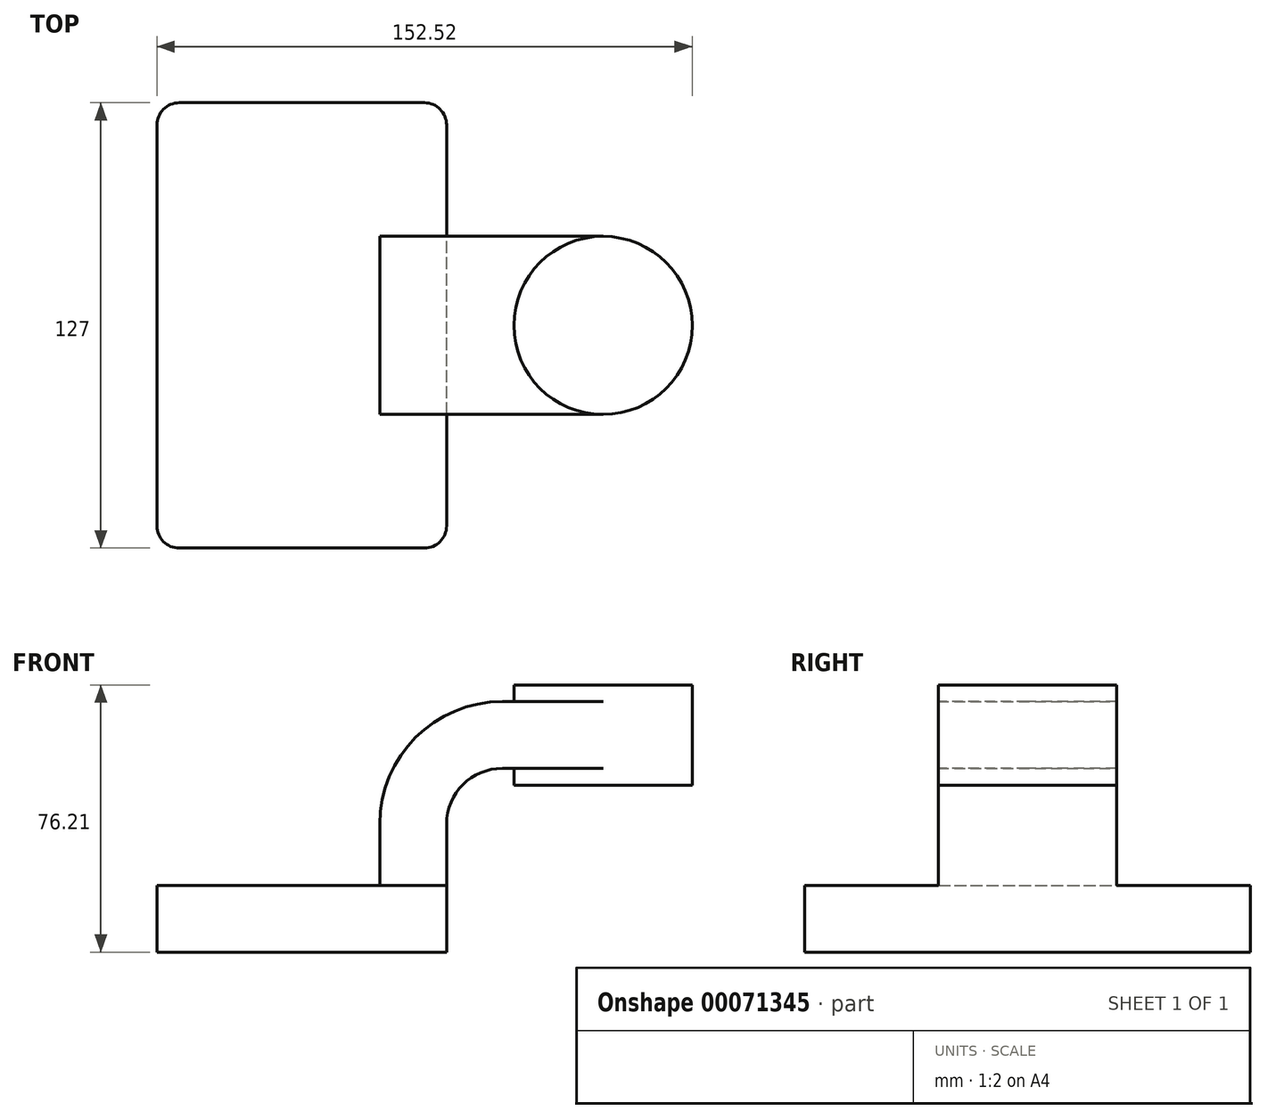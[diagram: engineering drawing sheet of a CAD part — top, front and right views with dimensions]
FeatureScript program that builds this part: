
annotation { "Feature Type Name" : "Feature", "Feature Type Description" : "" }
export const myFeature = defineFeature(function(context is Context, id is Id, definition is map)
    precondition{}
    {
        {
            var Q0;
            Q0=qCreatedBy(makeId("Front.planeOp"),FACE);
            var sketch = newSketch(context, id + "F0", { "sketchPlane" : qUnion([Q0])});
            skLineSegment(sketch, "E0.rect.bottom", {"start": v(41.28, -9.52) * mm, "end": v(-41.28, -9.53) * mm});
            skLineSegment(sketch, "E0.rect.top", {"start": v(41.28, 9.53) * mm, "end": v(-41.28, 9.53) * mm});
            skLineSegment(sketch, "E0.rect.left", {"start": v(41.28, -9.52) * mm, "end": v(41.28, 9.53) * mm});
            skLineSegment(sketch, "E0.rect.right", {"start": v(-41.28, -9.53) * mm, "end": v(-41.28, 9.53) * mm});
            skPoint(sketch, "E0.rect.middle", {"position": v(0, 0) * mm});
            skLineSegment(sketch, "E1.rect.bottom", {"start": v(111.25, 38.1) * mm, "end": v(60.45, 38.1) * mm});
            skLineSegment(sketch, "E1.rect.top", {"start": v(111.25, 66.68) * mm, "end": v(60.45, 66.68) * mm});
            skLineSegment(sketch, "E1.rect.left", {"start": v(111.25, 38.1) * mm, "end": v(111.25, 66.68) * mm});
            skLineSegment(sketch, "E1.rect.right", {"start": v(60.45, 38.1) * mm, "end": v(60.45, 66.68) * mm});
            skPoint(sketch, "E1.rect.middle", {"position": v(85.85, 52.39) * mm});
            skLineSegment(sketch, "E2", {"start": v(41.28, 9.53) * mm, "end": v(41.28, 27) * mm});
            skArc(sketch, "E3", {"start": v(41.27, 27) * mm, "mid": v(45.92, 38.23) * mm, "end": v(57.15, 42.88) * mm});
            skLineSegment(sketch, "E4", {"start": v(57.15, 42.88) * mm, "end": v(85.85, 42.88) * mm});
            skLineSegment(sketch, "E5.0", {"start": v(57.15, 61.93) * mm, "end": v(85.85, 61.93) * mm});
            skArc(sketch, "E5.1", {"start": v(22.23, 27) * mm, "mid": v(32.45, 51.7) * mm, "end": v(57.15, 61.93) * mm});
            skLineSegment(sketch, "E5.2", {"start": v(22.22, 9.53) * mm, "end": v(22.22, 27) * mm});
            skLineSegment(sketch, "E6", {"start": v(85.85, 38.1) * mm, "end": v(85.85, 66.68) * mm});
            skFitSpline(sketch, "E7", {"points": [v(-41.28, 9.53) * mm, v(57.15, 61.93) * mm], "startDerivative": vector(0.48, 72.5) * mm, "endDerivative": vector(122.57, -13.34) * mm});
            skSolve(sketch);
        }
        {
            var Q0;
            Q0=makeQuery(id+"F0.imprint","IMPRINT",FACE,{"disambiguationData":[TD([[makeQuery(id+"F0.imprint","IMPRINT",EDGE,{"derivedFrom":sQuery(id+"F0.wireOp",EDGE,"E0.rect.bottom")}),-1.0]])]});
            extrude(context, id + "F1", {"entities" : qUnion([Q0]), "depth" : 127 * mm, "symmetric" : true});
        }
        {
            var Q0;
            {var subQ1=sQuery(id+"F0.wireOp",EDGE,"E2");Q0=makeQuery(id+"F0.imprint","IMPRINT",FACE,{"disambiguationData":[TD([[makeQuery(id+"F0.imprint","IMPRINT",EDGE,{"derivedFrom":subQ1}),1.0]])]});}
            var Q1;
            {var subQ0=sQuery(id+"F0.wireOp",EDGE,"E4");var subQ1=sQuery(id+"F0.wireOp",EDGE,"E1.rect.right");var subQ2=makeQuery(id+"F0.imprint","INTERSECT",VERTEX,{"derivedFrom":[subQ1,subQ0]});Q1=makeQuery(id+"F0.imprint","IMPRINT",FACE,{"disambiguationData":[TD([[makeQuery(id+"F0.imprint","IMPRINT",EDGE,{"disambiguationData":[TD([[subQ2,-1.0]])],"derivedFrom":subQ1}),-1.0]])]});}
            extrude(context, id + "F2", {"entities" : qUnion([Q0, Q1]), "operationType" : NewBodyOperationType.ADD, "depth" : 50.8 * mm, "symmetric" : true});
        }
        {
            var Q0;
            Q0=makeQuery(id+"F0.imprint","IMPRINT",FACE,{"disambiguationData":[TD([[makeQuery(id+"F0.imprint","IMPRINT",EDGE,{"derivedFrom":sQuery(id+"F0.wireOp",EDGE,"E5.1")}),1.0]])]});
            extrude(context, id + "F3", {"entities" : qUnion([Q0]), "operationType" : NewBodyOperationType.ADD, "depth" : 15.88 * mm, "symmetric" : true});
        }
        {
            var Q0;
            {var subQ0=sQuery(id+"F0.wireOp",EDGE,"E1.rect.left");Q0=makeQuery(id+"F0.imprint","IMPRINT",FACE,{"disambiguationData":[TD([[makeQuery(id+"F0.imprint","IMPRINT",EDGE,{"derivedFrom":subQ0}),1.0]])]});}
            var Q1;
            Q1=sQuery(id+"F0.wireOp",EDGE,"E6");
            revolve(context, id + "F4", {"operationType" : NewBodyOperationType.ADD, "entities" : qUnion([Q0]), "axis" : qUnion([Q1]), "revolveType" : RevolveType.FULL});
        }
        {
            var Q0;
            Q0=makeQuery(id+"F1.opExtrude","CAP_EDGE",EDGE,{"disambiguationData":[OSD([sQuery(id+"F0.wireOp",EDGE,"E0.rect.left")])],"isStart":false});
            var Q1;
            Q1=makeQuery(id+"F1.opExtrude","CAP_EDGE",EDGE,{"disambiguationData":[OSD([sQuery(id+"F0.wireOp",EDGE,"E0.rect.left")])],"isStart":true});
            var Q2;
            Q2=makeQuery(id+"F1.opExtrude","CAP_EDGE",EDGE,{"disambiguationData":[OSD([sQuery(id+"F0.wireOp",EDGE,"E0.rect.right")])],"isStart":false});
            var Q3;
            Q3=makeQuery(id+"F1.opExtrude","CAP_EDGE",EDGE,{"disambiguationData":[OSD([sQuery(id+"F0.wireOp",EDGE,"E0.rect.right")])],"isStart":true});
            fillet(context, id + "F5", {"entities" : qUnion([Q0, Q1, Q2, Q3]), "radius" : 6.35 * mm, "tangentPropagation" : true, "allowEdgeOverflow" : false});
        }
    });
